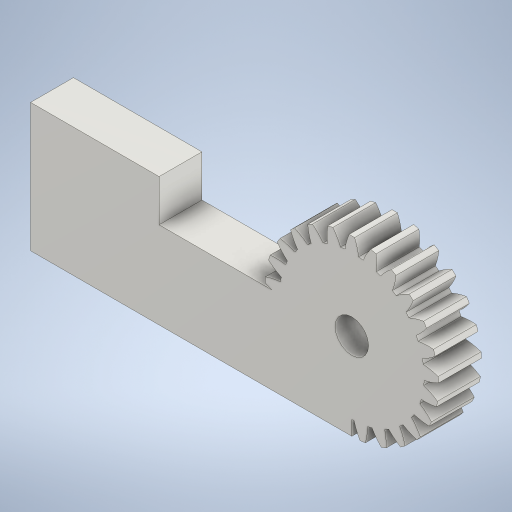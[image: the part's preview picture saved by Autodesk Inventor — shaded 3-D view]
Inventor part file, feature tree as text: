
AUTODESK INVENTOR PART (.ipt)
format: ipt  version: 2024 (Build 280153000, 153)  size: 971,776 bytes
history: native  units: mm (DEFAULTED — no unit token found)
features: extrude x3, plane x3, other x3, sketch x3, projected_geometry x2
ambient origin geometry x8: Origin, YZ Plane, XZ Plane, XY Plane, X Axis, Y Axis, Z Axis, Center Point
bodies: Solid1 (feature_tree)
feature tree (14):
  extrude  "Extrusion1"  Depth=6.666667mm TaperAngle=0.0deg
  plane  "Work Plane2"
  plane  "Work Plane8"
  plane  "Work Plane9"
  other  "Spur Gear"
  extrude  "Extrusion2"  Depth=10.0mm TaperAngle=0.0deg
  extrude  "Extrusion4"  Depth=30.0mm TaperAngle=0.0deg
  sketch  "Sketch1"  dims[d0=27.0mm d1=6.666667mm d2=0.0mm]
  other  "Srf1"
  sketch  "Sketch3"  dims[d3=25.0mm d4=10.0mm d5=0.0mm]
  projected_geometry  "Projected Loop1"
  sketch  "Sketch5"  dims[d16=25.0mm d17=0.0mm d34=1.256637mm d39=0.0mm d41=0.0mm d43=25.0mm d46=25.0mm d47=0.0mm d48=0.0mm d49=5.2mm d50=10.0mm d51=0.0mm d61=50.0mm d62=20.0mm d64=13.5mm d68=10.0mm d69=0.0mm d73=50.0mm d74=20.0mm d75=6.5mm d76=30.0mm]
  projected_geometry  "Projected Loop3"
  other  "Pitch Diameter"
